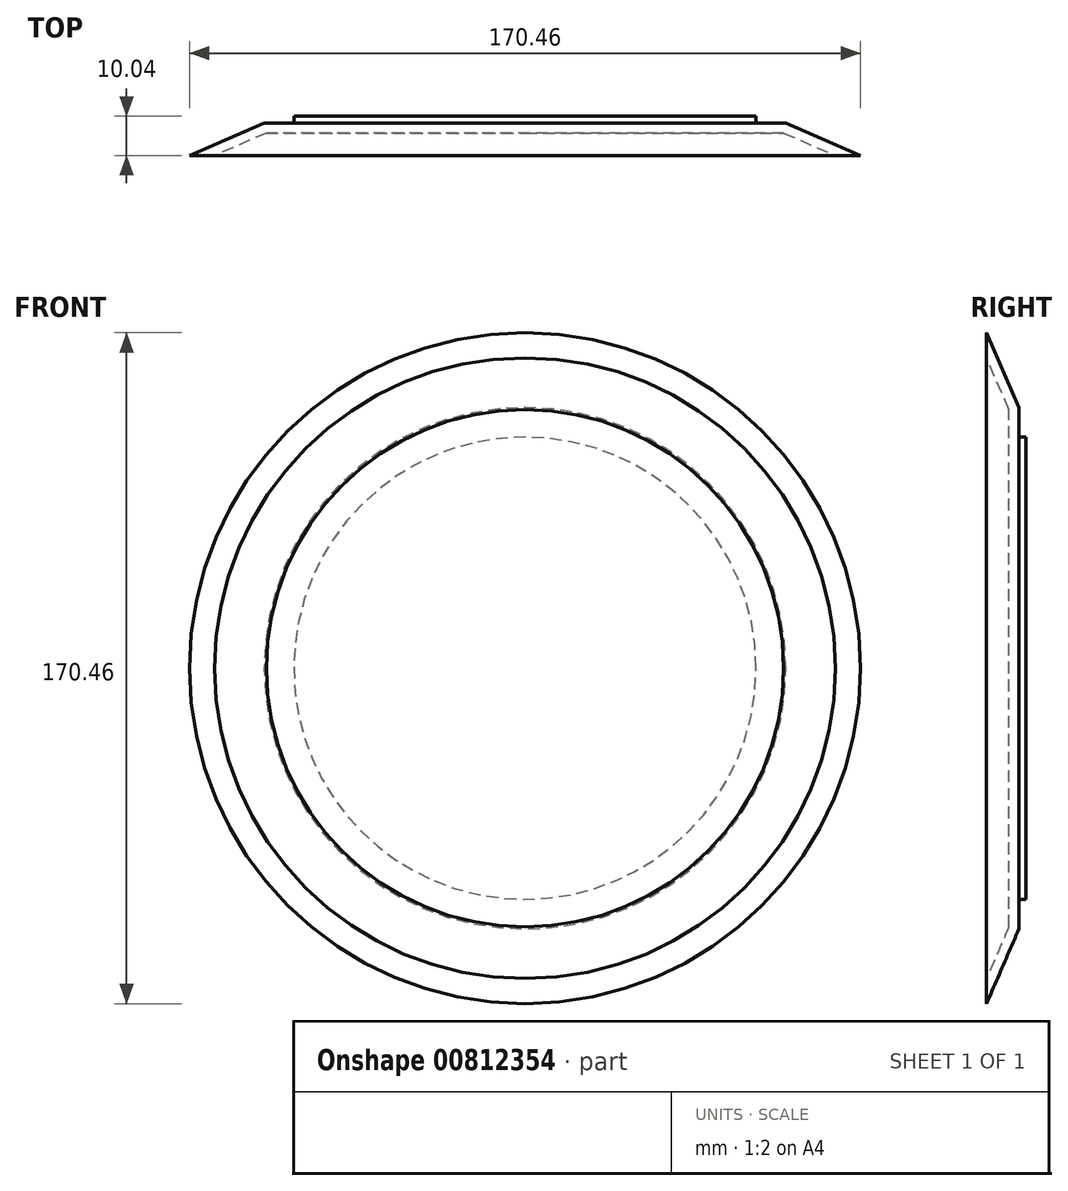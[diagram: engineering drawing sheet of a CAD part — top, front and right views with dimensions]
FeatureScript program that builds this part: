
annotation { "Feature Type Name" : "Feature", "Feature Type Description" : "" }
export const myFeature = defineFeature(function(context is Context, id is Id, definition is map)
    precondition{}
    {
        {
            var Q0;
            Q0=qCreatedBy(makeId("Top.planeOp"),FACE);
            var sketch = newSketch(context, id + "F0", { "sketchPlane" : qUnion([Q0])});
            skLineSegment(sketch, "E0", {"start": v(0, 49.23) * mm, "end": v(66.24, 49.23) * mm});
            skLineSegment(sketch, "E1", {"start": v(66.24, 49.23) * mm, "end": v(85.23, 40.97) * mm});
            skLineSegment(sketch, "E2", {"start": v(85.23, 40.97) * mm, "end": v(0, 40.97) * mm});
            skLineSegment(sketch, "E3", {"start": v(0, 40.97) * mm, "end": v(0, 49.23) * mm});
            skSolve(sketch);
        }
        {
            var Q0;
            Q0=makeQuery(id+"F0.imprint","IMPRINT",FACE,{"disambiguationData":[TD([[makeQuery(id+"F0.imprint","IMPRINT",EDGE,{"derivedFrom":sQuery(id+"F0.wireOp",EDGE,"E0")}),-1.0]])]});
            var Q1;
            Q1=sQuery(id+"F0.wireOp",EDGE,"E3");
            revolve(context, id + "F1", {"surfaceOperationType" : NewSurfaceOperationType.NEW, "entities" : qUnion([Q0]), "axis" : qUnion([Q1]), "revolveType" : RevolveType.FULL});
        }
        {
            var Q0;
            Q0=makeQuery(id+"F1.opRevolve","SWEPT_FACE",FACE,{"disambiguationData":[OSD([sQuery(id+"F0.wireOp",EDGE,"E2")])]});
            shell(context, id + "F2", {"entities" : qUnion([Q0]), "thickness" : 2.54 * mm});
        }
        {
            var Q0;
            Q0=makeQuery(id+"F1.opRevolve","SWEPT_FACE",FACE,{"disambiguationData":[OSD([sQuery(id+"F0.wireOp",EDGE,"E0")])]});
            var sketch = newSketch(context, id + "F3", { "sketchPlane" : qUnion([Q0])});
            skCircle(sketch, "E4", {"center": v(0, 0) * mm, "radius": 58.7 * mm});
            skSolve(sketch);
        }
        {
            var Q0;
            Q0=makeQuery(id+"F3.imprint","IMPRINT",FACE,{"disambiguationData":[TD([[makeQuery(id+"F3.imprint","IMPRINT",EDGE,{"derivedFrom":sQuery(id+"F3.wireOp",EDGE,"E4")}),1.0]])]});
            extrude(context, id + "F4", {"entities" : qUnion([Q0]), "operationType" : NewBodyOperationType.ADD, "depth" : 1.78 * mm, "offsetDistance" : 25.4 * mm});
        }
    });
